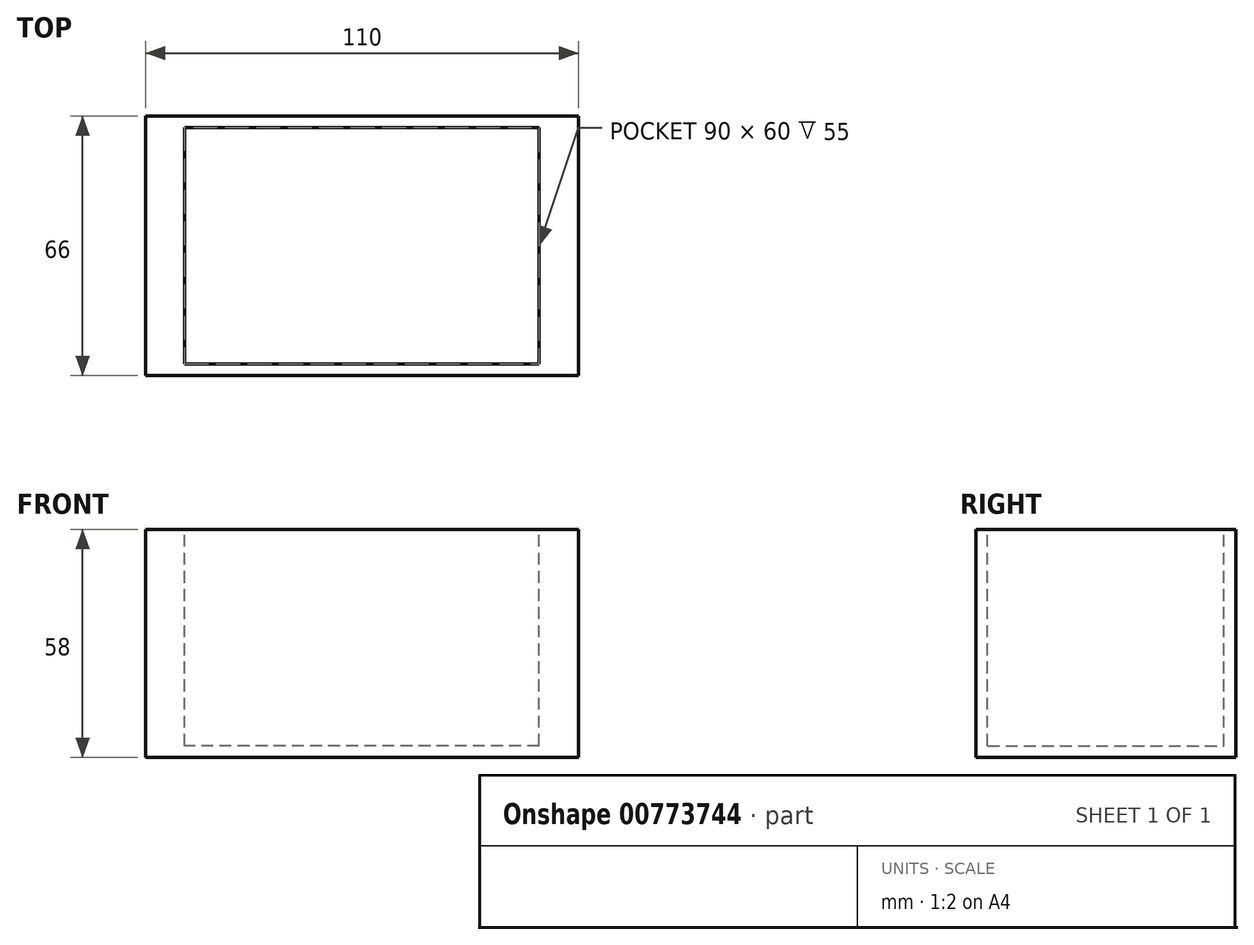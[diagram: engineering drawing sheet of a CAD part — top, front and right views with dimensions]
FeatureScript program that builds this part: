
annotation { "Feature Type Name" : "Feature", "Feature Type Description" : "" }
export const myFeature = defineFeature(function(context is Context, id is Id, definition is map)
    precondition{}
    {
        {
            var Q0;
            Q0=qCreatedBy(makeId("Top.planeOp"),FACE);
            var sketch = newSketch(context, id + "F0", { "sketchPlane" : qUnion([Q0])});
            skLineSegment(sketch, "E0.bottom", {"start": v(45, 30) * mm, "end": v(-45, 30) * mm});
            skLineSegment(sketch, "E0.top", {"start": v(45, -30) * mm, "end": v(-45, -30) * mm});
            skLineSegment(sketch, "E0.left", {"start": v(45, 30) * mm, "end": v(45, -30) * mm});
            skLineSegment(sketch, "E0.right", {"start": v(-45, 30) * mm, "end": v(-45, -30) * mm});
            skPoint(sketch, "E0.middle", {"position": v(0, 0) * mm});
            skLineSegment(sketch, "E1.0", {"start": v(48, 33) * mm, "end": v(-48, 33) * mm});
            skLineSegment(sketch, "E1.2", {"start": v(48, -33) * mm, "end": v(-48, -33) * mm});
            skLineSegment(sketch, "E2.1", {"start": v(55, 33) * mm, "end": v(55, -33) * mm});
            skLineSegment(sketch, "E2.3", {"start": v(-55, 33) * mm, "end": v(-55, -33) * mm});
            skLineSegment(sketch, "E3", {"start": v(-48, 33) * mm, "end": v(-55, 33) * mm});
            skLineSegment(sketch, "E4", {"start": v(48, 33) * mm, "end": v(55, 33) * mm});
            skLineSegment(sketch, "E5", {"start": v(48, -33) * mm, "end": v(55, -33) * mm});
            skLineSegment(sketch, "E6", {"start": v(-48, -33) * mm, "end": v(-55, -33) * mm});
            skSolve(sketch);
        }
        {
            var Q0;
            Q0=makeQuery(id+"F0.imprint","IMPRINT",FACE,{"disambiguationData":[TD([[makeQuery(id+"F0.imprint","IMPRINT",EDGE,{"derivedFrom":sQuery(id+"F0.wireOp",EDGE,"E0.bottom")}),1.0]])]});
            var Q1;
            Q1=makeQuery(id+"F0.imprint","IMPRINT",FACE,{"disambiguationData":[TD([[makeQuery(id+"F0.imprint","IMPRINT",EDGE,{"derivedFrom":sQuery(id+"F0.wireOp",EDGE,"E0.bottom")}),-1.0]])]});
            extrude(context, id + "F1", {"entities" : qUnion([Q0, Q1]), "depth" : 58 * mm, "offsetDistance" : 25 * mm});
        }
        {
            var Q0;
            Q0=makeQuery(id+"F1.opExtrude","CAP_FACE",FACE,{"disambiguationData":[OSD([sQuery(id+"F0.wireOp",EDGE,"E1.0"),sQuery(id+"F0.wireOp",EDGE,"E1.2"),sQuery(id+"F0.wireOp",EDGE,"E2.1"),sQuery(id+"F0.wireOp",EDGE,"E2.3"),sQuery(id+"F0.wireOp",EDGE,"E3"),sQuery(id+"F0.wireOp",EDGE,"E4"),sQuery(id+"F0.wireOp",EDGE,"E5"),sQuery(id+"F0.wireOp",EDGE,"E6")])],"isStart":false});
            var sketch = newSketch(context, id + "F2", { "sketchPlane" : qUnion([Q0])});
            skLineSegment(sketch, "E7.bottom", {"start": v(45, -30) * mm, "end": v(-45, -30) * mm});
            skLineSegment(sketch, "E7.top", {"start": v(45, 30) * mm, "end": v(-45, 30) * mm});
            skLineSegment(sketch, "E7.left", {"start": v(45, -30) * mm, "end": v(45, 30) * mm});
            skLineSegment(sketch, "E7.right", {"start": v(-45, -30) * mm, "end": v(-45, 30) * mm});
            skPoint(sketch, "E7.middle", {"position": v(0, 0) * mm});
            skSolve(sketch);
        }
        {
            var Q0;
            Q0=makeQuery(id+"F2.imprint","IMPRINT",FACE,{"disambiguationData":[TD([[makeQuery(id+"F2.imprint","IMPRINT",EDGE,{"derivedFrom":sQuery(id+"F2.wireOp",EDGE,"E7.bottom")}),-1.0]])]});
            extrude(context, id + "F3", {"entities" : qUnion([Q0]), "operationType" : NewBodyOperationType.ADD, "oppositeDirection" : true, "depth" : 55 * mm, "offsetDistance" : 25 * mm});
        }
        {
            var Q0;
            Q0 = qSketchRegion(id + "F2", true);
            extrude(context, id + "F4", {"entities" : qUnion([Q0]), "operationType" : NewBodyOperationType.REMOVE, "oppositeDirection" : true, "depth" : 55 * mm, "offsetDistance" : 25 * mm});
        }
    });
